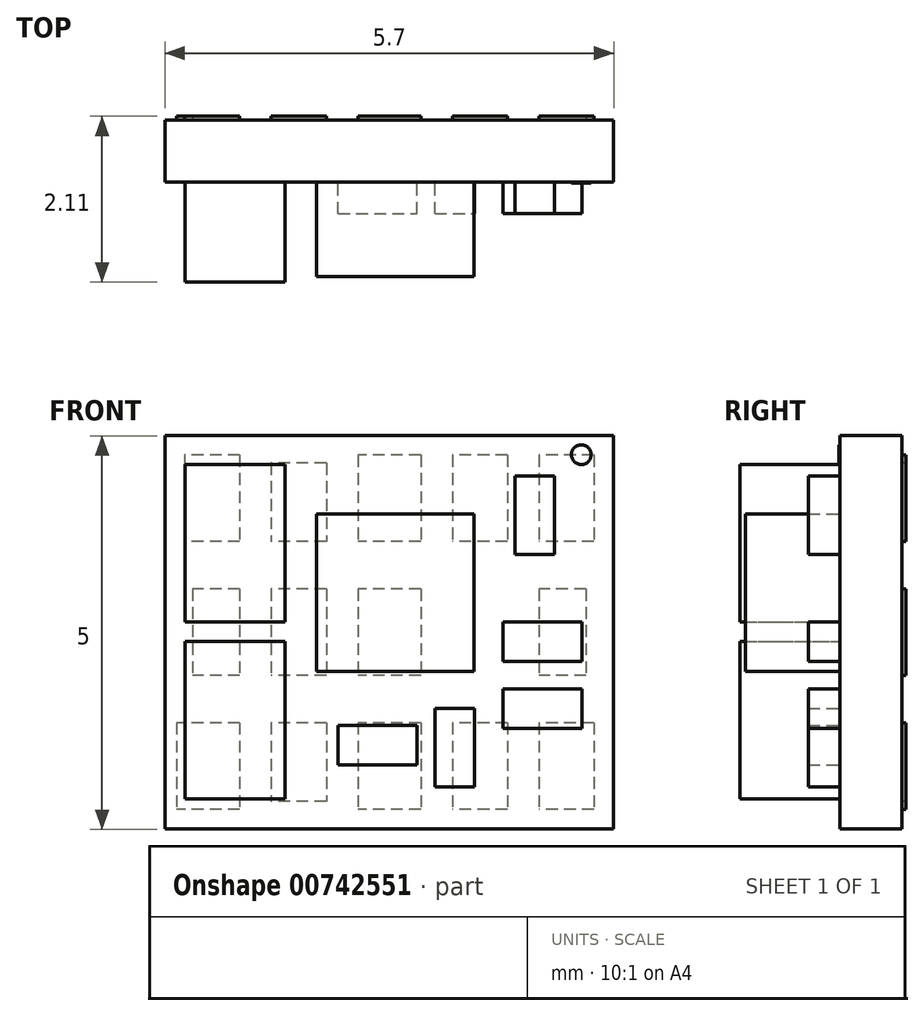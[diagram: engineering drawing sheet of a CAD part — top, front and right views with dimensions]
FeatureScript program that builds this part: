
annotation { "Feature Type Name" : "Feature", "Feature Type Description" : "" }
export const myFeature = defineFeature(function(context is Context, id is Id, definition is map)
    precondition{}
    {
        {
            var Q0;
            Q0=qCreatedBy(makeId("Front.planeOp"),FACE);
            var sketch = newSketch(context, id + "F0", { "sketchPlane" : qUnion([Q0])});
            skLineSegment(sketch, "E0.bottom", {"start": v(-0.68, -0.12) * mm, "end": v(5.02, -0.12) * mm});
            skLineSegment(sketch, "E0.top", {"start": v(-0.68, -5.12) * mm, "end": v(5.02, -5.12) * mm});
            skLineSegment(sketch, "E0.left", {"start": v(-0.68, -0.12) * mm, "end": v(-0.68, -5.12) * mm});
            skLineSegment(sketch, "E0.right", {"start": v(5.02, -0.12) * mm, "end": v(5.02, -5.12) * mm});
            skSolve(sketch);
        }
        {
            var Q0;
            Q0=makeQuery(id+"F0.imprint","IMPRINT",FACE,{"disambiguationData":[TD([[makeQuery(id+"F0.imprint","IMPRINT",EDGE,{"derivedFrom":sQuery(id+"F0.wireOp",EDGE,"E0.bottom")}),-1.0]])]});
            extrude(context, id + "F1", {"entities" : qUnion([Q0]), "depth" : 0.79 * mm, "offsetDistance" : 25 * mm});
        }
        {
            var Q0;
            Q0=makeQuery(id+"F1.opExtrude","CAP_FACE",FACE,{"disambiguationData":[OSD([sQuery(id+"F0.wireOp",EDGE,"E0.bottom"),sQuery(id+"F0.wireOp",EDGE,"E0.top"),sQuery(id+"F0.wireOp",EDGE,"E0.left"),sQuery(id+"F0.wireOp",EDGE,"E0.right")])],"isStart":false});
            var sketch = newSketch(context, id + "F2", { "sketchPlane" : qUnion([Q0])});
            skLineSegment(sketch, "E1.bottom", {"start": v(1.24, -1.12) * mm, "end": v(3.24, -1.12) * mm});
            skLineSegment(sketch, "E1.top", {"start": v(1.24, -3.12) * mm, "end": v(3.24, -3.12) * mm});
            skLineSegment(sketch, "E1.left", {"start": v(1.24, -1.12) * mm, "end": v(1.24, -3.12) * mm});
            skLineSegment(sketch, "E1.right", {"start": v(3.24, -1.12) * mm, "end": v(3.24, -3.12) * mm});
            skSolve(sketch);
        }
        {
            var Q0;
            Q0=makeQuery(id+"F2.imprint","IMPRINT",FACE,{"disambiguationData":[TD([[makeQuery(id+"F2.imprint","IMPRINT",EDGE,{"derivedFrom":sQuery(id+"F2.wireOp",EDGE,"E1.bottom")}),-1.0]])]});
            extrude(context, id + "F3", {"entities" : qUnion([Q0]), "operationType" : NewBodyOperationType.ADD, "depth" : 1.2 * mm, "offsetDistance" : 25 * mm});
        }
        {
            var Q0;
            Q0=makeQuery(id+"F1.opExtrude","CAP_FACE",FACE,{"disambiguationData":[OSD([sQuery(id+"F0.wireOp",EDGE,"E0.bottom"),sQuery(id+"F0.wireOp",EDGE,"E0.top"),sQuery(id+"F0.wireOp",EDGE,"E0.left"),sQuery(id+"F0.wireOp",EDGE,"E0.right")])],"isStart":false});
            var sketch = newSketch(context, id + "F4", { "sketchPlane" : qUnion([Q0])});
            skLineSegment(sketch, "E2.bottom", {"start": v(-0.43, -0.48) * mm, "end": v(0.84, -0.48) * mm});
            skLineSegment(sketch, "E2.top", {"start": v(-0.43, -2.48) * mm, "end": v(0.84, -2.48) * mm});
            skLineSegment(sketch, "E2.left", {"start": v(-0.43, -0.48) * mm, "end": v(-0.43, -2.48) * mm});
            skLineSegment(sketch, "E2.right", {"start": v(0.84, -0.48) * mm, "end": v(0.84, -2.48) * mm});
            skLineSegment(sketch, "E3.top", {"start": v(-0.43, -0.98) * mm, "end": v(0.84, -0.98) * mm});
            skLineSegment(sketch, "E3.left", {"start": v(-0.43, -0.48) * mm, "end": v(-0.43, -0.98) * mm});
            skLineSegment(sketch, "E3.right", {"start": v(0.84, -0.48) * mm, "end": v(0.84, -0.98) * mm});
            skLineSegment(sketch, "E4.left", {"start": v(-0.43, -2.04) * mm, "end": v(-0.43, -2.48) * mm});
            skLineSegment(sketch, "E4.right", {"start": v(0.84, -2.04) * mm, "end": v(0.84, -2.48) * mm});
            skLineSegment(sketch, "E5.top", {"start": v(-0.43, -1.98) * mm, "end": v(0.84, -1.98) * mm});
            skLineSegment(sketch, "E5.left", {"start": v(-0.43, -2.48) * mm, "end": v(-0.43, -1.98) * mm});
            skLineSegment(sketch, "E5.right", {"start": v(0.84, -2.48) * mm, "end": v(0.84, -1.98) * mm});
            skLineSegment(sketch, "E6.bottom", {"start": v(-0.42, -2.73) * mm, "end": v(0.85, -2.73) * mm});
            skLineSegment(sketch, "E6.top", {"start": v(-0.42, -4.73) * mm, "end": v(0.85, -4.73) * mm});
            skLineSegment(sketch, "E6.left", {"start": v(-0.42, -2.73) * mm, "end": v(-0.42, -4.73) * mm});
            skLineSegment(sketch, "E6.right", {"start": v(0.85, -2.73) * mm, "end": v(0.85, -4.73) * mm});
            skLineSegment(sketch, "E7.top", {"start": v(-0.42, -3.23) * mm, "end": v(0.85, -3.23) * mm});
            skLineSegment(sketch, "E7.left", {"start": v(-0.42, -2.73) * mm, "end": v(-0.42, -3.23) * mm});
            skLineSegment(sketch, "E7.right", {"start": v(0.85, -2.73) * mm, "end": v(0.85, -3.23) * mm});
            skLineSegment(sketch, "E8.top", {"start": v(-0.42, -4.23) * mm, "end": v(0.85, -4.23) * mm});
            skLineSegment(sketch, "E8.left", {"start": v(-0.42, -4.73) * mm, "end": v(-0.42, -4.23) * mm});
            skLineSegment(sketch, "E8.right", {"start": v(0.85, -4.73) * mm, "end": v(0.85, -4.23) * mm});
            skSolve(sketch);
        }
        {
            var Q0;
            Q0 = qSketchRegion(id + "F4", true);
            extrude(context, id + "F5", {"entities" : qUnion([Q0]), "operationType" : NewBodyOperationType.ADD, "depth" : 1.27 * mm, "offsetDistance" : 25 * mm});
        }
        {
            var Q0;
            Q0=makeQuery(id+"F1.opExtrude","CAP_FACE",FACE,{"disambiguationData":[OSD([sQuery(id+"F0.wireOp",EDGE,"E0.bottom"),sQuery(id+"F0.wireOp",EDGE,"E0.top"),sQuery(id+"F0.wireOp",EDGE,"E0.left"),sQuery(id+"F0.wireOp",EDGE,"E0.right")])],"isStart":false});
            var sketch = newSketch(context, id + "F6", { "sketchPlane" : qUnion([Q0])});
            skLineSegment(sketch, "E9.bottom", {"start": v(1.52, -3.8) * mm, "end": v(2.52, -3.8) * mm});
            skLineSegment(sketch, "E9.top", {"start": v(1.52, -4.3) * mm, "end": v(2.52, -4.3) * mm});
            skLineSegment(sketch, "E9.left", {"start": v(1.52, -3.8) * mm, "end": v(1.52, -4.3) * mm});
            skLineSegment(sketch, "E9.right", {"start": v(2.52, -3.8) * mm, "end": v(2.52, -4.3) * mm});
            skLineSegment(sketch, "E10.bottom", {"start": v(2.75, -4.58) * mm, "end": v(3.25, -4.58) * mm});
            skLineSegment(sketch, "E10.top", {"start": v(2.75, -3.58) * mm, "end": v(3.25, -3.58) * mm});
            skLineSegment(sketch, "E10.left", {"start": v(2.75, -4.58) * mm, "end": v(2.75, -3.58) * mm});
            skLineSegment(sketch, "E10.right", {"start": v(3.25, -4.58) * mm, "end": v(3.25, -3.58) * mm});
            skLineSegment(sketch, "E11.bottom", {"start": v(3.61, -3.33) * mm, "end": v(4.61, -3.33) * mm});
            skLineSegment(sketch, "E11.top", {"start": v(3.61, -3.83) * mm, "end": v(4.61, -3.83) * mm});
            skLineSegment(sketch, "E11.left", {"start": v(3.61, -3.33) * mm, "end": v(3.61, -3.83) * mm});
            skLineSegment(sketch, "E11.right", {"start": v(4.61, -3.33) * mm, "end": v(4.61, -3.83) * mm});
            skLineSegment(sketch, "E12.bottom", {"start": v(3.61, -2.48) * mm, "end": v(4.61, -2.48) * mm});
            skLineSegment(sketch, "E12.top", {"start": v(3.61, -2.98) * mm, "end": v(4.61, -2.98) * mm});
            skLineSegment(sketch, "E12.left", {"start": v(3.61, -2.48) * mm, "end": v(3.61, -2.98) * mm});
            skLineSegment(sketch, "E12.right", {"start": v(4.61, -2.48) * mm, "end": v(4.61, -2.98) * mm});
            skLineSegment(sketch, "E13.bottom", {"start": v(3.76, -0.63) * mm, "end": v(4.26, -0.63) * mm});
            skLineSegment(sketch, "E13.top", {"start": v(3.76, -1.63) * mm, "end": v(4.26, -1.63) * mm});
            skLineSegment(sketch, "E13.left", {"start": v(3.76, -0.63) * mm, "end": v(3.76, -1.63) * mm});
            skLineSegment(sketch, "E13.right", {"start": v(4.26, -0.63) * mm, "end": v(4.26, -1.63) * mm});
            skSolve(sketch);
        }
        {
            var Q0;
            Q0 = qSketchRegion(id + "F6", true);
            extrude(context, id + "F7", {"entities" : qUnion([Q0]), "operationType" : NewBodyOperationType.ADD, "depth" : 0.4 * mm, "offsetDistance" : 25 * mm});
        }
        {
            var Q0;
            Q0=makeQuery(id+"F1.opExtrude","CAP_FACE",FACE,{"disambiguationData":[OSD([sQuery(id+"F0.wireOp",EDGE,"E0.bottom"),sQuery(id+"F0.wireOp",EDGE,"E0.top"),sQuery(id+"F0.wireOp",EDGE,"E0.left"),sQuery(id+"F0.wireOp",EDGE,"E0.right")])],"isStart":false});
            var sketch = newSketch(context, id + "F8", { "sketchPlane" : qUnion([Q0])});
            skCircle(sketch, "E14", {"center": v(4.6, -0.36) * mm, "radius": 0.12 * mm});
            skSolve(sketch);
        }
        {
            var Q0;
            Q0=makeQuery(id+"F8.imprint","IMPRINT",FACE,{"disambiguationData":[TD([[makeQuery(id+"F8.imprint","IMPRINT",EDGE,{"derivedFrom":sQuery(id+"F8.wireOp",EDGE,"E14")}),1.0]])]});
            extrude(context, id + "F9", {"entities" : qUnion([Q0]), "operationType" : NewBodyOperationType.ADD, "depth" : 0.01 * mm, "offsetDistance" : 25 * mm});
        }
        {
            var Q0;
            Q0=makeQuery(id+"F1.opExtrude","CAP_FACE",FACE,{"disambiguationData":[OSD([sQuery(id+"F0.wireOp",EDGE,"E0.bottom"),sQuery(id+"F0.wireOp",EDGE,"E0.top"),sQuery(id+"F0.wireOp",EDGE,"E0.left"),sQuery(id+"F0.wireOp",EDGE,"E0.right")])],"isStart":true});
            var sketch = newSketch(context, id + "F10", { "sketchPlane" : qUnion([Q0])});
            skLineSegment(sketch, "E15.bottom", {"start": v(-4.77, -3.77) * mm, "end": v(-4.07, -3.77) * mm});
            skLineSegment(sketch, "E15.top", {"start": v(-4.77, -4.87) * mm, "end": v(-4.07, -4.87) * mm});
            skLineSegment(sketch, "E15.left", {"start": v(-4.77, -3.77) * mm, "end": v(-4.77, -4.87) * mm});
            skLineSegment(sketch, "E15.right", {"start": v(-4.07, -3.77) * mm, "end": v(-4.07, -4.87) * mm});
            skLineSegment(sketch, "E16.bottom", {"start": v(-4.67, -2.07) * mm, "end": v(-4.07, -2.07) * mm});
            skLineSegment(sketch, "E16.top", {"start": v(-4.67, -3.17) * mm, "end": v(-4.07, -3.17) * mm});
            skLineSegment(sketch, "E16.left", {"start": v(-4.67, -2.07) * mm, "end": v(-4.67, -3.17) * mm});
            skLineSegment(sketch, "E16.right", {"start": v(-4.07, -2.07) * mm, "end": v(-4.07, -3.17) * mm});
            skLineSegment(sketch, "E17.bottom", {"start": v(-2.57, -2.07) * mm, "end": v(-1.77, -2.07) * mm});
            skLineSegment(sketch, "E17.top", {"start": v(-2.57, -3.17) * mm, "end": v(-1.77, -3.17) * mm});
            skLineSegment(sketch, "E17.left", {"start": v(-2.57, -2.07) * mm, "end": v(-2.57, -3.17) * mm});
            skLineSegment(sketch, "E17.right", {"start": v(-1.77, -2.07) * mm, "end": v(-1.77, -3.17) * mm});
            skLineSegment(sketch, "E18.bottom", {"start": v(-1.37, -2.07) * mm, "end": v(-0.67, -2.07) * mm});
            skLineSegment(sketch, "E18.top", {"start": v(-1.37, -3.17) * mm, "end": v(-0.67, -3.17) * mm});
            skLineSegment(sketch, "E18.left", {"start": v(-1.37, -2.07) * mm, "end": v(-1.37, -3.17) * mm});
            skLineSegment(sketch, "E18.right", {"start": v(-0.67, -2.07) * mm, "end": v(-0.67, -3.17) * mm});
            skLineSegment(sketch, "E19.bottom", {"start": v(-3.67, -3.77) * mm, "end": v(-2.97, -3.77) * mm});
            skLineSegment(sketch, "E19.top", {"start": v(-3.67, -4.87) * mm, "end": v(-2.97, -4.87) * mm});
            skLineSegment(sketch, "E19.left", {"start": v(-3.67, -3.77) * mm, "end": v(-3.67, -4.87) * mm});
            skLineSegment(sketch, "E19.right", {"start": v(-2.97, -3.77) * mm, "end": v(-2.97, -4.87) * mm});
            skLineSegment(sketch, "E20.bottom", {"start": v(-2.57, -3.77) * mm, "end": v(-1.77, -3.77) * mm});
            skLineSegment(sketch, "E20.top", {"start": v(-2.57, -4.87) * mm, "end": v(-1.77, -4.87) * mm});
            skLineSegment(sketch, "E20.left", {"start": v(-2.57, -3.77) * mm, "end": v(-2.57, -4.87) * mm});
            skLineSegment(sketch, "E20.right", {"start": v(-1.77, -3.77) * mm, "end": v(-1.77, -4.87) * mm});
            skLineSegment(sketch, "E21.bottom", {"start": v(-1.37, -3.77) * mm, "end": v(-0.67, -3.77) * mm});
            skLineSegment(sketch, "E21.top", {"start": v(-1.37, -4.77) * mm, "end": v(-0.67, -4.77) * mm});
            skLineSegment(sketch, "E21.left", {"start": v(-1.37, -3.77) * mm, "end": v(-1.37, -4.77) * mm});
            skLineSegment(sketch, "E21.right", {"start": v(-0.67, -3.77) * mm, "end": v(-0.67, -4.77) * mm});
            skLineSegment(sketch, "E22.bottom", {"start": v(-4.77, -0.37) * mm, "end": v(-4.07, -0.37) * mm});
            skLineSegment(sketch, "E22.top", {"start": v(-4.77, -1.47) * mm, "end": v(-4.07, -1.47) * mm});
            skLineSegment(sketch, "E22.left", {"start": v(-4.77, -0.37) * mm, "end": v(-4.77, -1.47) * mm});
            skLineSegment(sketch, "E22.right", {"start": v(-4.07, -0.37) * mm, "end": v(-4.07, -1.47) * mm});
            skLineSegment(sketch, "E23.bottom", {"start": v(-3.67, -0.37) * mm, "end": v(-2.97, -0.37) * mm});
            skLineSegment(sketch, "E23.top", {"start": v(-3.67, -1.47) * mm, "end": v(-2.97, -1.47) * mm});
            skLineSegment(sketch, "E23.left", {"start": v(-3.67, -0.37) * mm, "end": v(-3.67, -1.47) * mm});
            skLineSegment(sketch, "E23.right", {"start": v(-2.97, -0.37) * mm, "end": v(-2.97, -1.47) * mm});
            skLineSegment(sketch, "E24.bottom", {"start": v(-2.57, -0.37) * mm, "end": v(-1.77, -0.37) * mm});
            skLineSegment(sketch, "E24.top", {"start": v(-2.57, -1.47) * mm, "end": v(-1.77, -1.47) * mm});
            skLineSegment(sketch, "E24.left", {"start": v(-2.57, -0.37) * mm, "end": v(-2.57, -1.47) * mm});
            skLineSegment(sketch, "E24.right", {"start": v(-1.77, -0.37) * mm, "end": v(-1.77, -1.47) * mm});
            skLineSegment(sketch, "E25.bottom", {"start": v(-1.37, -0.47) * mm, "end": v(-0.67, -0.47) * mm});
            skLineSegment(sketch, "E25.top", {"start": v(-1.37, -1.47) * mm, "end": v(-0.67, -1.47) * mm});
            skLineSegment(sketch, "E25.left", {"start": v(-1.37, -0.47) * mm, "end": v(-1.37, -1.47) * mm});
            skLineSegment(sketch, "E25.right", {"start": v(-0.67, -0.47) * mm, "end": v(-0.67, -1.47) * mm});
            skLineSegment(sketch, "E26.bottom", {"start": v(-0.27, -3.77) * mm, "end": v(0.53, -3.77) * mm});
            skLineSegment(sketch, "E26.top", {"start": v(-0.27, -4.87) * mm, "end": v(0.53, -4.87) * mm});
            skLineSegment(sketch, "E26.left", {"start": v(-0.27, -3.77) * mm, "end": v(-0.27, -4.87) * mm});
            skLineSegment(sketch, "E26.right", {"start": v(0.53, -3.77) * mm, "end": v(0.53, -4.87) * mm});
            skLineSegment(sketch, "E27.bottom", {"start": v(-0.27, -2.07) * mm, "end": v(0.33, -2.07) * mm});
            skLineSegment(sketch, "E27.top", {"start": v(-0.27, -3.17) * mm, "end": v(0.33, -3.17) * mm});
            skLineSegment(sketch, "E27.left", {"start": v(-0.27, -2.07) * mm, "end": v(-0.27, -3.17) * mm});
            skLineSegment(sketch, "E27.right", {"start": v(0.33, -2.07) * mm, "end": v(0.33, -3.17) * mm});
            skLineSegment(sketch, "E28.bottom", {"start": v(-0.27, -0.37) * mm, "end": v(0.43, -0.37) * mm});
            skLineSegment(sketch, "E28.top", {"start": v(-0.27, -1.47) * mm, "end": v(0.43, -1.47) * mm});
            skLineSegment(sketch, "E28.left", {"start": v(-0.27, -0.37) * mm, "end": v(-0.27, -1.47) * mm});
            skLineSegment(sketch, "E28.right", {"start": v(0.43, -0.37) * mm, "end": v(0.43, -1.47) * mm});
            skSolve(sketch);
        }
        {
            var Q0;
            Q0 = qSketchRegion(id + "F10", true);
            extrude(context, id + "F11", {"entities" : qUnion([Q0]), "operationType" : NewBodyOperationType.ADD, "depth" : 0.05 * mm, "offsetDistance" : 25 * mm});
        }
    });
